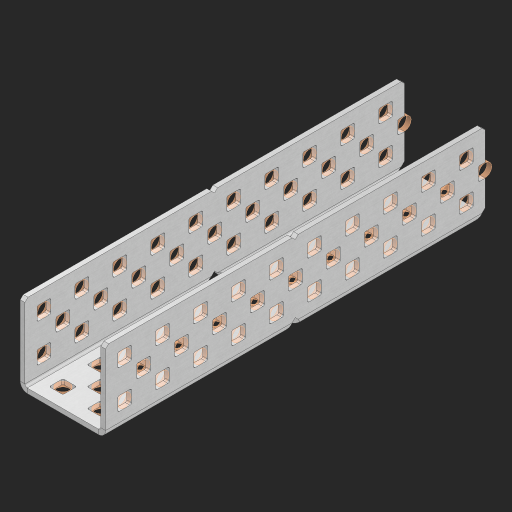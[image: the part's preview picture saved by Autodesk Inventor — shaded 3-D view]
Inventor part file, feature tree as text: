
AUTODESK INVENTOR PART (.ipt)
format: ipt  version: 2023 (Build 270158000, 158)  size: 1,402,880 bytes
history: native  units: in
note: dims shown in document units (in); Inventor stores cm internally (conversion verified against a paired STEP export)
features: other x126, extrude x118, sheet_metal_op x8, sketch x7, mirror x3, pattern_linear x2, chamfer x1
ambient origin geometry x8: Origin, YZ Plane, XZ Plane, XY Plane, X Axis, Y Axis, Z Axis, Center Point
bodies: Solid1 (feature_tree), Body (feature_tree)
feature tree (265):
  sheet_metal_op  "Flanges"
  sheet_metal_op  "Body Pattern"
  pattern_linear  "Center Pattern"  Spacing1=1.0in  [1 undecoded]
  other  "Arc Length"
  mirror  "Notch Mirror"
  pattern_linear  "Notch Pattern"  Spacing1=0.25in  [1 undecoded]
  other  "Diagonal Plane"
  mirror  "Flange 1"
  mirror  "Flange 2"
  chamfer  "End Chamfer"
  sketch  "Sketch1"  dims[d0=1.0in]
  other  "Plate1"
  sketch  "Sketch2"  dims[d1=5.0in]
  other  "Plate2"
  sheet_metal_op  "Bend1"
  sheet_metal_op  "Corner1"
  sketch  "Sketch8"  dims[d2=0.0625in]
  sketch  "Sketch9"  dims[d3=0.0625in]
  other  "Srf91"
  sheet_metal_op  "Body Pattern Sketch"
  other  "Srf92"
  sketch  "Sketch13"  dims[d4=0.0312in]
  sketch  "Sketch15"  dims[d5=0.125in]
  sketch  "Sketch16"  dims[d6=0.0625in d7=1.0in d8=90.0deg d9=0.0312in d10=0.25in d11=0.0625in d12=0.0625in d49=0.182in d50=0.02in d52=0.25in d53=0.0625in d54=0.0in d55=0.172in d56=1.0in d57=0.0in d60=3.937in d62=0.5in d63=0.7874in d65=0.5in d85=0.1473in d86=0.1782in d88=0.04in d89=0.0625in d90=0.0in d91=0.04in d92=0.0491in d95=2.5in d96=0.04in d97=0.25in d98=45.0deg d99=0.25in d102=2.497in d106=0.182in d107=0.02in d108=0.5in d110=0.0625in d111=0.0in d112=0.172in d113=0.5in d114=0.0in d117=0.5in d118=0.5in d131=0.25in d132=0.25in]
  other  "Srf786"
  other  "Srf889"
  other  "Srf890"
  other  "Srf891"
  other  "Srf892"
  other  "Srf893"
  other  "Srf894"
  other  "Srf895"
  other  "Srf896"
  other  "Srf996"
  other  "Srf1315"
  other  "Srf1316"
  other  "Srf1317"
  other  "Srf1325"
  other  "Srf1326"
  other  "Srf1327"
  other  "Srf1328"
  other  "Srf1329"
  other  "Srf1330"
  other  "Srf1331"
  other  "Srf1332"
  other  "Srf1338"
  other  "Srf1374"
  other  "Srf1375"
  other  "Srf1376"
  other  "Srf1384"
  other  "Srf1385"
  other  "Srf1386"
  other  "Srf1387"
  other  "Srf1388"
  other  "Srf1389"
  other  "Srf1390"
  other  "Srf1391"
  other  "Srf1397"
  other  "Srf1433"
  other  "Srf1434"
  other  "Srf1473"
  other  "Srf1474"
  other  "Srf1475"
  other  "Srf1476"
  other  "Srf1477"
  other  "Srf1478"
  other  "Srf1479"
  other  "Srf1480"
  other  "Srf1481"
  other  "Srf1482"
  other  "Srf1500"
  other  "Srf1501"
  other  "Srf1502"
  other  "Srf1503"
  other  "Srf1504"
  other  "Srf1505"
  other  "Srf1506"
  other  "Srf1507"
  other  "Srf1508"
  other  "Srf1509"
  other  "Srf1510"
  other  "Srf1511"
  other  "Srf1512"
  other  "Srf1513"
  other  "Srf1514"
  other  "Srf1515"
  other  "Srf1516"
  other  "Srf1517"
  other  "Srf1538"
  other  "Srf1539"
  other  "Srf1540"
  other  "Srf1541"
  other  "Srf1542"
  other  "Srf1543"
  other  "Srf1544"
  other  "Srf1545"
  other  "Srf1546"
  other  "Srf1547"
  other  "Srf1548"
  other  "Srf1549"
  other  "Srf1550"
  other  "Srf1551"
  other  "Srf1552"
  other  "Srf1553"
  other  "Srf1554"
  other  "Srf1555"
  other  "Srf1576"
  other  "Srf1577"
  other  "Srf1578"
  other  "Srf1579"
  other  "Srf1580"
  other  "Srf1581"
  other  "Srf1582"
  other  "Srf1583"
  other  "Srf1584"
  other  "Srf1585"
  other  "Srf1586"
  other  "Srf1587"
  other  "Srf1588"
  other  "Srf1589"
  other  "Srf1590"
  other  "Srf1591"
  other  "Srf1592"
  other  "Srf1593"
  other  "Srf1614"
  other  "Srf1615"
  other  "Srf1616"
  other  "Srf1617"
  other  "Srf1618"
  other  "Srf1619"
  other  "Srf1620"
  other  "Srf1621"
  other  "Srf1622"
  other  "Srf1623"
  other  "Srf1624"
  other  "Srf1625"
  other  "Srf1626"
  other  "Srf1627"
  other  "Srf1628"
  other  "Srf1629"
  other  "Srf1630"
  other  "Srf1631"
  sheet_metal_op  "Body Stamp"
  sheet_metal_op  "Body Circle"
  other  "Center Stamp"
  other  "Center Circle"
  sheet_metal_op  "Notch"
  extrude  "ExtrusionSrf92"  Depth=0.0625in
  extrude  "ExtrusionSrf889"  Depth=0.0625in
  extrude  "ExtrusionSrf890"  Depth=0.5in
  extrude  "ExtrusionSrf891"  Depth=0.02in
  extrude  "ExtrusionSrf892"  Depth=0.5in
  extrude  "ExtrusionSrf893"  Depth=0.0625in
  extrude  "ExtrusionSrf894"  TaperAngle=0.0deg  [1 undecoded]
  extrude  "ExtrusionSrf895"  Depth=0.5in
  extrude  "ExtrusionSrf896"  Depth=1.0in TaperAngle=0.0deg
  extrude  "ExtrusionSrf996"  Depth=0.5in
  extrude  "ExtrusionSrf1315"  Depth=0.5in
  extrude  "ExtrusionSrf1316"  Depth=0.5in
  extrude  "ExtrusionSrf1355"  Depth=0.5in
  extrude  "ExtrusionSrf1356"  Depth=0.5in
  extrude  "ExtrusionSrf1357"  Depth=0.0625in
  extrude  "ExtrusionSrf1358"  TaperAngle=0.0deg  [1 undecoded]
  extrude  "ExtrusionSrf1359"  Depth=0.5in
  extrude  "ExtrusionSrf1360"  Depth=0.5in
  extrude  "ExtrusionSrf1361"  Depth=2.5in
  extrude  "ExtrusionSrf1362"  Depth=0.5in TaperAngle=45.0deg
  extrude  "ExtrusionSrf1363"  Depth=0.5in
  extrude  "ExtrusionSrf1364"  Depth=0.5in
  extrude  "ExtrusionSrf1374"  Depth=0.5in
  extrude  "ExtrusionSrf1375"  Depth=0.02in
  extrude  "ExtrusionSrf1414"  Depth=0.5in
  extrude  "ExtrusionSrf1415"  Depth=0.0625in
  extrude  "ExtrusionSrf1416"  TaperAngle=0.0deg  [1 undecoded]
  extrude  "ExtrusionSrf1417"  Depth=0.5in
  extrude  "ExtrusionSrf1418"  Depth=0.5in TaperAngle=0.0deg
  extrude  "ExtrusionSrf1419"  Depth=0.5in
  extrude  "ExtrusionSrf1420"  Depth=0.5in
  extrude  "ExtrusionSrf1421"  Depth=0.5in
  extrude  "ExtrusionSrf1422"  Depth=0.5in
  extrude  "ExtrusionSrf1423"  [1 undecoded]
  extrude  "ExtrusionSrf1433"  [1 undecoded]
  extrude  "ExtrusionSrf1434"  [1 undecoded]
  extrude  "ExtrusionSrf1473"  [1 undecoded]
  extrude  "ExtrusionSrf1474"  [1 undecoded]
  extrude  "ExtrusionSrf1475"  [1 undecoded]
  extrude  "ExtrusionSrf1476"  [1 undecoded]
  extrude  "ExtrusionSrf1477"  [1 undecoded]
  extrude  "ExtrusionSrf1478"  [1 undecoded]
  extrude  "ExtrusionSrf1479"  [1 undecoded]
  extrude  "ExtrusionSrf1480"  [1 undecoded]
  extrude  "ExtrusionSrf1481"  [1 undecoded]
  extrude  "ExtrusionSrf1482"  [1 undecoded]
  extrude  "ExtrusionSrf1500"  [1 undecoded]
  extrude  "ExtrusionSrf1501"  [1 undecoded]
  extrude  "ExtrusionSrf1502"  [1 undecoded]
  extrude  "ExtrusionSrf1503"  [1 undecoded]
  extrude  "ExtrusionSrf1504"  [1 undecoded]
  extrude  "ExtrusionSrf1505"  [1 undecoded]
  extrude  "ExtrusionSrf1506"  [1 undecoded]
  extrude  "ExtrusionSrf1507"  [1 undecoded]
  extrude  "ExtrusionSrf1508"  [1 undecoded]
  extrude  "ExtrusionSrf1509"  [1 undecoded]
  extrude  "ExtrusionSrf1510"  [1 undecoded]
  extrude  "ExtrusionSrf1511"  [1 undecoded]
  extrude  "ExtrusionSrf1512"  [1 undecoded]
  extrude  "ExtrusionSrf1513"  [1 undecoded]
  extrude  "ExtrusionSrf1514"  [1 undecoded]
  extrude  "ExtrusionSrf1515"  [1 undecoded]
  extrude  "ExtrusionSrf1516"  [1 undecoded]
  extrude  "ExtrusionSrf1517"  [1 undecoded]
  extrude  "ExtrusionSrf1538"  [1 undecoded]
  extrude  "ExtrusionSrf1539"  [1 undecoded]
  extrude  "ExtrusionSrf1540"  [1 undecoded]
  extrude  "ExtrusionSrf1541"  [1 undecoded]
  extrude  "ExtrusionSrf1542"  [1 undecoded]
  extrude  "ExtrusionSrf1543"  [1 undecoded]
  extrude  "ExtrusionSrf1544"  [1 undecoded]
  extrude  "ExtrusionSrf1545"  [1 undecoded]
  extrude  "ExtrusionSrf1546"  [1 undecoded]
  extrude  "ExtrusionSrf1547"  [1 undecoded]
  extrude  "ExtrusionSrf1548"  [1 undecoded]
  extrude  "ExtrusionSrf1549"  [1 undecoded]
  extrude  "ExtrusionSrf1550"  [1 undecoded]
  extrude  "ExtrusionSrf1551"  [1 undecoded]
  extrude  "ExtrusionSrf1552"  [1 undecoded]
  extrude  "ExtrusionSrf1553"  [1 undecoded]
  extrude  "ExtrusionSrf1554"  [1 undecoded]
  extrude  "ExtrusionSrf1555"  [1 undecoded]
  extrude  "ExtrusionSrf1576"  [1 undecoded]
  extrude  "ExtrusionSrf1577"  [1 undecoded]
  extrude  "ExtrusionSrf1578"  [1 undecoded]
  extrude  "ExtrusionSrf1579"  [1 undecoded]
  extrude  "ExtrusionSrf1580"  [1 undecoded]
  extrude  "ExtrusionSrf1581"  [1 undecoded]
  extrude  "ExtrusionSrf1582"  [1 undecoded]
  extrude  "ExtrusionSrf1583"  [1 undecoded]
  extrude  "ExtrusionSrf1584"  [1 undecoded]
  extrude  "ExtrusionSrf1585"  [1 undecoded]
  extrude  "ExtrusionSrf1586"  [1 undecoded]
  extrude  "ExtrusionSrf1587"  [1 undecoded]
  extrude  "ExtrusionSrf1588"  [1 undecoded]
  extrude  "ExtrusionSrf1589"  [1 undecoded]
  extrude  "ExtrusionSrf1590"  [1 undecoded]
  extrude  "ExtrusionSrf1591"  [1 undecoded]
  extrude  "ExtrusionSrf1592"  [1 undecoded]
  extrude  "ExtrusionSrf1593"  [1 undecoded]
  extrude  "ExtrusionSrf1614"  [1 undecoded]
  extrude  "ExtrusionSrf1615"  [1 undecoded]
  extrude  "ExtrusionSrf1616"  [1 undecoded]
  extrude  "ExtrusionSrf1617"  [1 undecoded]
  extrude  "ExtrusionSrf1618"  [1 undecoded]
  extrude  "ExtrusionSrf1619"  [1 undecoded]
  extrude  "ExtrusionSrf1620"  [1 undecoded]
  extrude  "ExtrusionSrf1621"  [1 undecoded]
  extrude  "ExtrusionSrf1622"  [1 undecoded]
  extrude  "ExtrusionSrf1623"  [1 undecoded]
  extrude  "ExtrusionSrf1624"  [1 undecoded]
  extrude  "ExtrusionSrf1625"  [1 undecoded]
  extrude  "ExtrusionSrf1626"  [1 undecoded]
  extrude  "ExtrusionSrf1627"  [1 undecoded]
  extrude  "ExtrusionSrf1628"  [1 undecoded]
  extrude  "ExtrusionSrf1629"  [1 undecoded]
  extrude  "ExtrusionSrf1630"  [1 undecoded]
  extrude  "ExtrusionSrf1631"  [1 undecoded]
note: 90 required parameter values undecoded (feature->parameter linkage not recoverable at this tier; creation-order binding heuristic only, values carry confidence <= 0.55)
